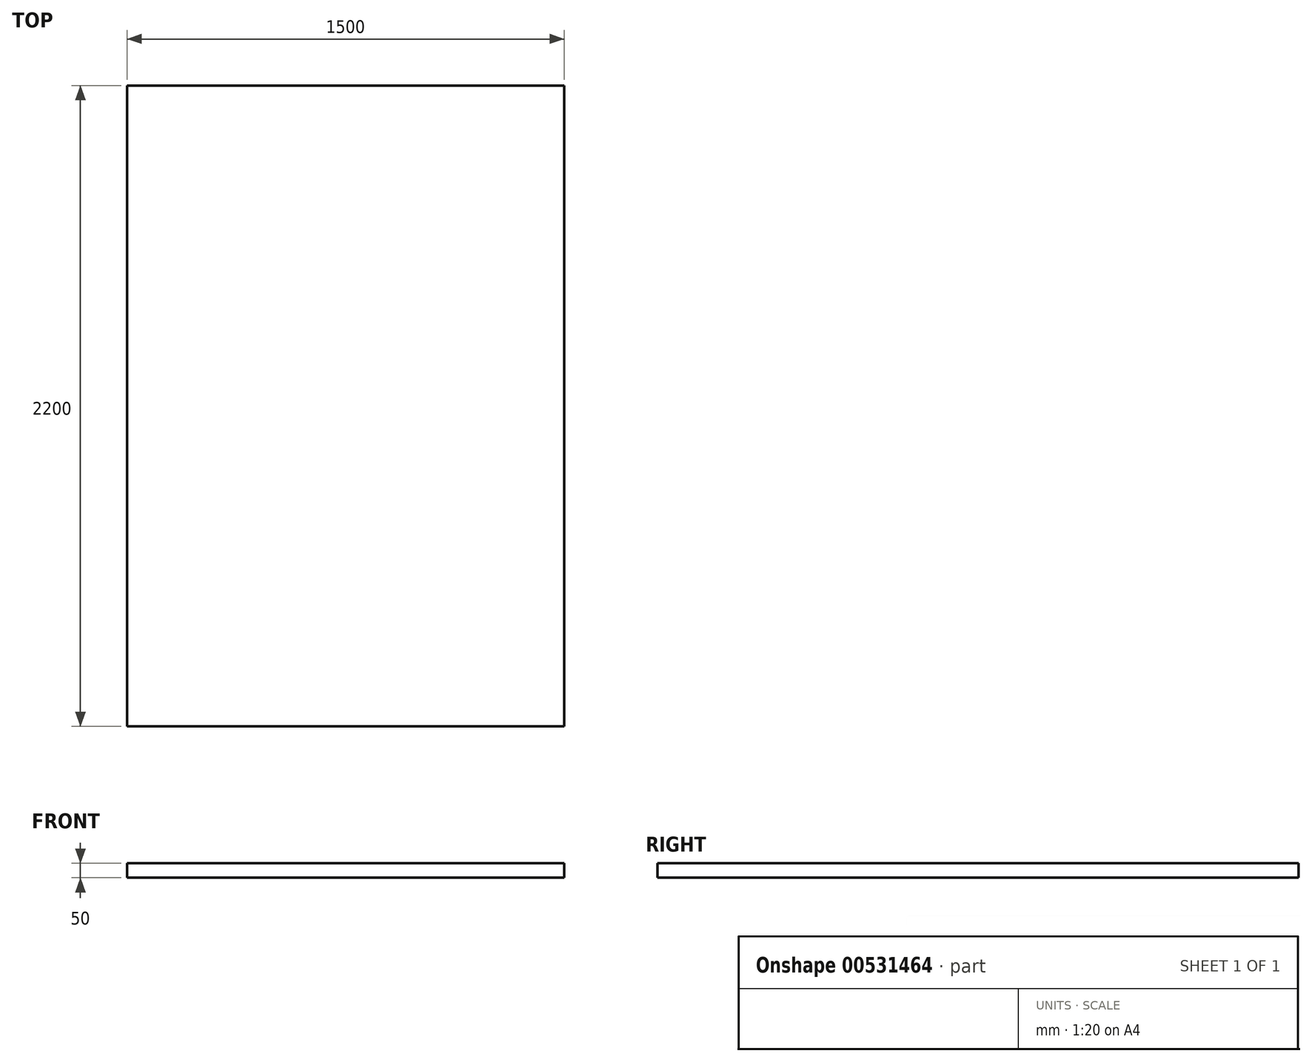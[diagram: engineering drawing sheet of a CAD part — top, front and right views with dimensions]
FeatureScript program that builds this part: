
annotation { "Feature Type Name" : "Feature", "Feature Type Description" : "" }
export const myFeature = defineFeature(function(context is Context, id is Id, definition is map)
    precondition{}
    {
        {
            var Q0;
            Q0=qCreatedBy(makeId("Top.planeOp"),FACE);
            var sketch = newSketch(context, id + "F0", { "sketchPlane" : qUnion([Q0])});
            skLineSegment(sketch, "E0.bottom", {"start": v(0, 0) * mm, "end": v(-1500, 0) * mm});
            skLineSegment(sketch, "E0.top", {"start": v(0, 2200) * mm, "end": v(-1500, 2200) * mm});
            skLineSegment(sketch, "E0.left", {"start": v(0, 0) * mm, "end": v(0, 2200) * mm});
            skLineSegment(sketch, "E0.right", {"start": v(-1500, 0) * mm, "end": v(-1500, 2200) * mm});
            skSolve(sketch);
        }
        {
            var Q0;
            Q0 = qSketchRegion(id + "F0", true);
            extrude(context, id + "F1", {"entities" : qUnion([Q0]), "depth" : 50 * mm, "offsetDistance" : 25 * mm});
        }
    });
